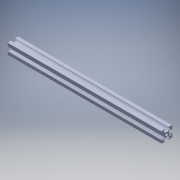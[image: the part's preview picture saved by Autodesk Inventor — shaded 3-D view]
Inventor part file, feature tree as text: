
AUTODESK INVENTOR PART (.ipt)
format: ipt  version: 2018 (Build 220112000, 112)  size: 371,200 bytes
history: native  units: in
note: dims shown in document units (in); Inventor stores cm internally (conversion verified against a paired STEP export)
features: extrude x1, sketch x1, projected_geometry x1, fillet x1
ambient origin geometry x8: Origin, YZ Plane, XZ Plane, XY Plane, X Axis, Y Axis, Z Axis, Center Point
bodies: Solid1 (feature_tree)
feature tree (4):
  extrude  "Extrusion2"  [1 undecoded]
  sketch  "Sketch3"  dims[d2=7.4803in d3=0.0in]
  projected_geometry  "Projected Loop2"
  fillet  "Fillet5"  [1 undecoded]
note: 2 required parameter values undecoded (feature->parameter linkage not recoverable at this tier; creation-order binding heuristic only, values carry confidence <= 0.55)
